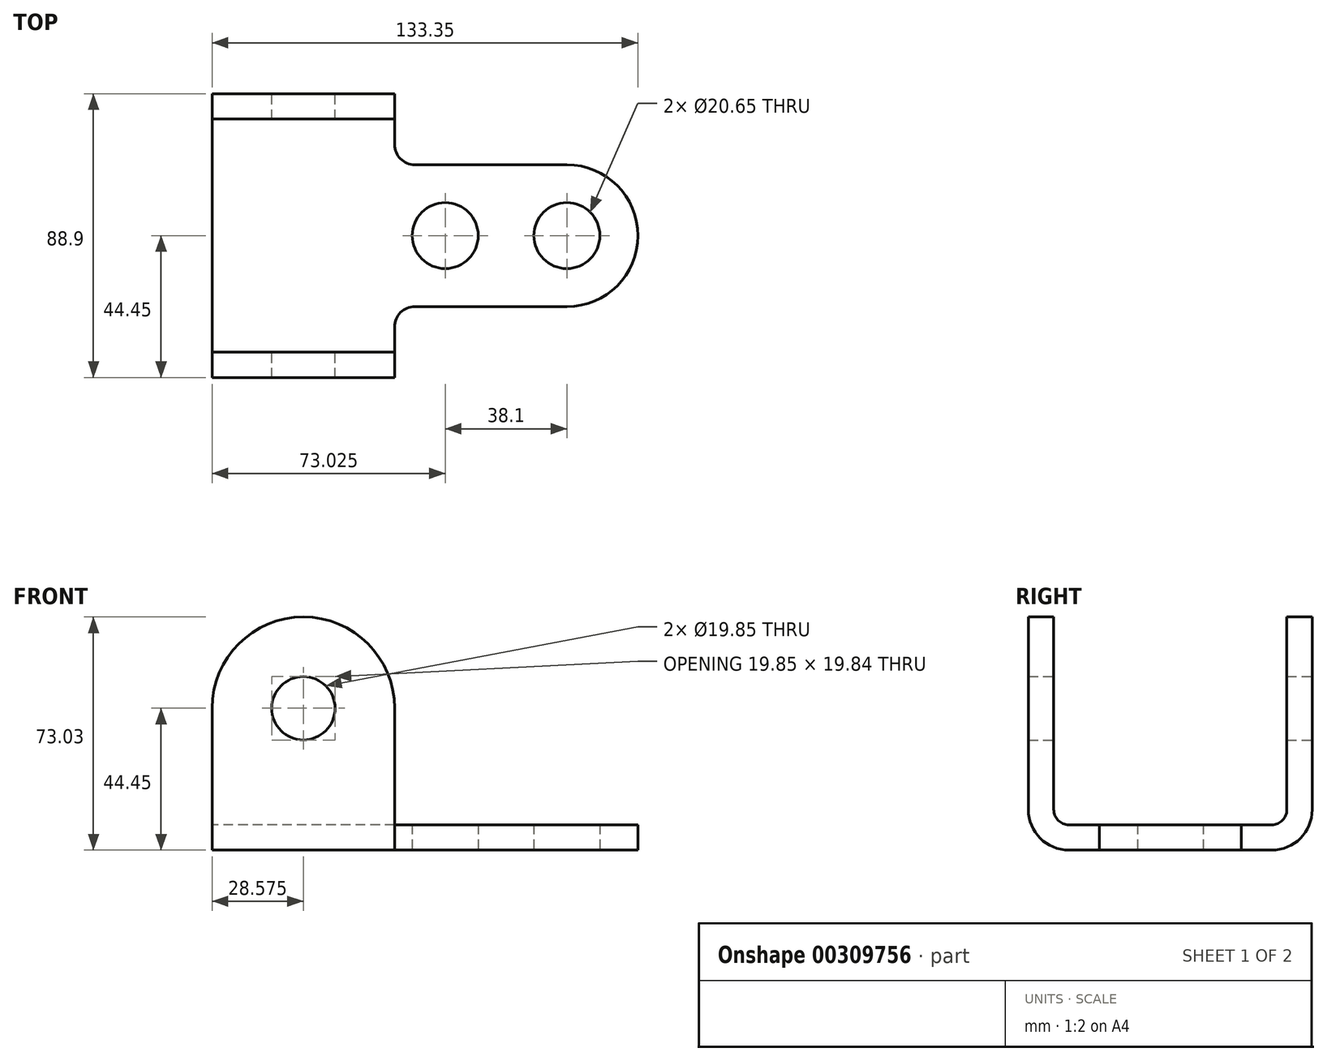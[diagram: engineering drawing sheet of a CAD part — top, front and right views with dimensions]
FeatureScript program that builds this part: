
annotation { "Feature Type Name" : "Feature", "Feature Type Description" : "" }
export const myFeature = defineFeature(function(context is Context, id is Id, definition is map)
    precondition{}
    {
        {
            var Q0;
            Q0=qCreatedBy(makeId("Front.planeOp"),FACE);
            var sketch = newSketch(context, id + "F0", { "sketchPlane" : qUnion([Q0])});
            skLineSegment(sketch, "E0.bottom", {"start": v(0, 0) * mm, "end": v(57.15, 0) * mm});
            skLineSegment(sketch, "E0.top", {"start": v(28.57, 73.03) * mm, "end": v(28.57, 73.03) * mm});
            skLineSegment(sketch, "E0.left", {"start": v(0, 0) * mm, "end": v(0, 44.45) * mm});
            skLineSegment(sketch, "E0.right", {"start": v(57.15, 0) * mm, "end": v(57.15, 44.45) * mm});
            skPoint(sketch, "E1.visualSharp", {"position": v(0, 73.03) * mm});
            skArc(sketch, "E1.filletArc", {"start": v(28.57, 73.03) * mm, "mid": v(8.37, 64.66) * mm, "end": v(0, 44.45) * mm});
            skPoint(sketch, "E2.visualSharp", {"position": v(57.15, 73.03) * mm});
            skArc(sketch, "E2.filletArc", {"start": v(57.15, 44.45) * mm, "mid": v(48.78, 64.66) * mm, "end": v(28.57, 73.03) * mm});
            skCircle(sketch, "E3", {"center": v(28.57, 44.45) * mm, "radius": 9.92 * mm});
            skSolve(sketch);
        }
        {
            var Q0;
            Q0 = qSketchRegion(id + "F0", true);
            extrude(context, id + "F1", {"entities" : qUnion([Q0]), "endBound" : BoundingType.SYMMETRIC, "depth" : 88.9 * mm});
        }
        {
            var Q0;
            Q0=qCreatedBy(makeId("Top.planeOp"),FACE);
            var sketch = newSketch(context, id + "F2", { "sketchPlane" : qUnion([Q0])});
            skLineSegment(sketch, "E4.bottom", {"start": v(0, -22.22) * mm, "end": v(111.12, -22.22) * mm});
            skLineSegment(sketch, "E4.top", {"start": v(0, 22.23) * mm, "end": v(111.12, 22.23) * mm});
            skLineSegment(sketch, "E4.left", {"start": v(0, -22.23) * mm, "end": v(0, 22.23) * mm});
            skLineSegment(sketch, "E4.right", {"start": v(133.35, 0) * mm, "end": v(133.35, 0) * mm});
            skPoint(sketch, "E5.visualSharp", {"position": v(133.35, 22.22) * mm});
            skArc(sketch, "E5.filletArc", {"start": v(133.35, 0) * mm, "mid": v(126.84, 15.72) * mm, "end": v(111.12, 22.23) * mm});
            skPoint(sketch, "E6.visualSharp", {"position": v(133.35, -22.22) * mm});
            skArc(sketch, "E6.filletArc", {"start": v(111.12, -22.22) * mm, "mid": v(126.84, -15.72) * mm, "end": v(133.35, 0) * mm});
            skCircle(sketch, "E7", {"center": v(111.12, 0) * mm, "radius": 10.33 * mm});
            skCircle(sketch, "E8", {"center": v(73.03, 0) * mm, "radius": 10.33 * mm});
            skSolve(sketch);
        }
        {
            var Q0;
            Q0 = qSketchRegion(id + "F2", true);
            extrude(context, id + "F3", {"entities" : qUnion([Q0]), "operationType" : NewBodyOperationType.ADD, "depth" : 7.94 * mm});
        }
        {
            var Q0;
            Q0=qCreatedBy(makeId("Right.planeOp"),FACE);
            var sketch = newSketch(context, id + "F4", { "sketchPlane" : qUnion([Q0])});
            skLineSegment(sketch, "E9.bottom", {"start": v(-36.51, 84.14) * mm, "end": v(36.51, 84.14) * mm});
            skLineSegment(sketch, "E9.top", {"start": v(-36.51, 7.94) * mm, "end": v(36.51, 7.94) * mm});
            skLineSegment(sketch, "E9.left", {"start": v(-36.51, 84.14) * mm, "end": v(-36.51, 7.94) * mm});
            skLineSegment(sketch, "E9.right", {"start": v(36.51, 84.14) * mm, "end": v(36.51, 7.94) * mm});
            skSolve(sketch);
        }
        {
            var Q0;
            Q0 = qSketchRegion(id + "F4", true);
            extrude(context, id + "F5", {"entities" : qUnion([Q0]), "operationType" : NewBodyOperationType.REMOVE, "endBound" : BoundingType.THROUGH_ALL, "depth" : 25.4 * mm});
        }
        {
            var Q0;
            Q0=makeQuery(id+"F1.opExtrude","CAP_EDGE",EDGE,{"disambiguationData":[OSD([sQuery(id+"F0.wireOp",EDGE,"E0.bottom")])],"isStart":false});
            var Q1;
            Q1=makeQuery(id+"F1.opExtrude","CAP_EDGE",EDGE,{"disambiguationData":[OSD([sQuery(id+"F0.wireOp",EDGE,"E0.bottom")])],"isStart":true});
            fillet(context, id + "F6", {"entities" : qUnion([Q0, Q1]), "radius" : 12.7 * mm, "tangentPropagation" : true, "allowEdgeOverflow" : false});
        }
        {
            var Q0;
            Q0=makeQuery(id+"F5.boolean.opBoolean","COPY",EDGE,{"derivedFrom":makeQuery(id+"F5.opExtrude","SWEPT_EDGE",EDGE,{"disambiguationData":[OSD([sQuery(id+"F4.wireOp",EDGE,"E9.top"),sQuery(id+"F4.wireOp",EDGE,"E9.right")])]})});
            var Q1;
            Q1=makeQuery(id+"F5.boolean.opBoolean","COPY",EDGE,{"derivedFrom":makeQuery(id+"F5.opExtrude","SWEPT_EDGE",EDGE,{"disambiguationData":[OSD([sQuery(id+"F4.wireOp",EDGE,"E9.top"),sQuery(id+"F4.wireOp",EDGE,"E9.left")])]})});
            fillet(context, id + "F7", {"entities" : qUnion([Q0, Q1]), "radius" : 4.76 * mm, "tangentPropagation" : true, "allowEdgeOverflow" : false});
        }
        {
            var Q0;
            Q0=makeQuery(id+"F3.boolean.opBoolean","INTERSECT",EDGE,{"derivedFrom":[makeQuery(id+"F1.opExtrude","SWEPT_FACE",FACE,{"disambiguationData":[OSD([sQuery(id+"F0.wireOp",EDGE,"E0.right")])]}),makeQuery(id+"F3.opExtrude","SWEPT_FACE",FACE,{"disambiguationData":[OSD([sQuery(id+"F2.wireOp",EDGE,"E4.bottom")])]})]});
            var Q1;
            Q1=makeQuery(id+"F3.boolean.opBoolean","INTERSECT",EDGE,{"derivedFrom":[makeQuery(id+"F1.opExtrude","SWEPT_FACE",FACE,{"disambiguationData":[OSD([sQuery(id+"F0.wireOp",EDGE,"E0.right")])]}),makeQuery(id+"F3.opExtrude","SWEPT_FACE",FACE,{"disambiguationData":[OSD([sQuery(id+"F2.wireOp",EDGE,"E4.top")])]})]});
            fillet(context, id + "F8", {"entities" : qUnion([Q0, Q1]), "radius" : 6.35 * mm, "tangentPropagation" : true, "allowEdgeOverflow" : false});
        }
    });
